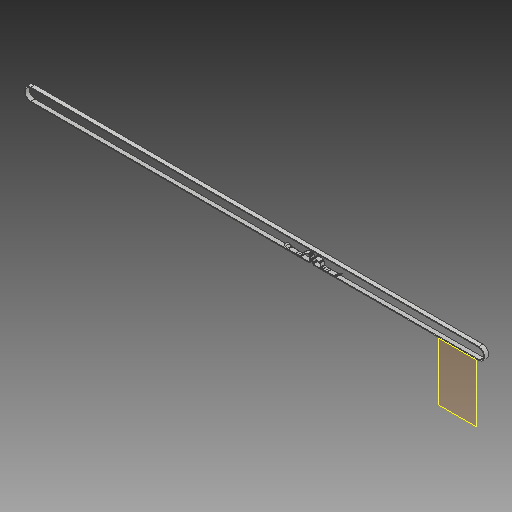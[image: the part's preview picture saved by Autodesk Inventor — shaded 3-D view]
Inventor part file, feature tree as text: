
AUTODESK INVENTOR PART (.ipt)
format: ipt  version: 2017 (Build 210142000, 142)  size: 205,824 bytes
history: native  units: mm
features: other x3, sketch x1, plane x1
ambient origin geometry x8: Origin, YZ Plane, XZ Plane, XY Plane, X Axis, Y Axis, Z Axis, Center Point
bodies: Solid1 (feature_tree)
feature tree (5):
  other  "XBELT.ipt"
  other  "Solid2::XBELT.ipt"
  other  "TaggingFeature1"
  sketch  "Sketch1"  dims[d0=10.0mm]
  plane  "Work Plane1"
